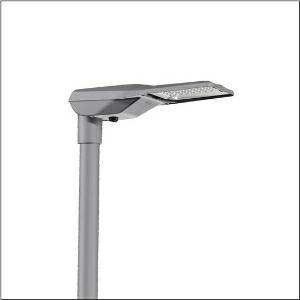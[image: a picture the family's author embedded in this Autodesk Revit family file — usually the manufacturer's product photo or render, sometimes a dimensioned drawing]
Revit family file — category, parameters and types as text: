
# Revit family: streetlight_sl_21_iq_mini___p0_8ab_5xe2r31u08gb_eb08
name_source: partatom
category: Lighting Fixtures
units: mm (PartAtom-declared; Revit-internal decimal feet)

## family parameters
Cut with Voids When Loaded = No
Host = Face
Light Source = No
Part Type = Normal
Room Calculation Point = No
Round Connector Dimension = Use Diameter
Shared = No

## types (1)
- --- (1 x LED, 5200 lm, 39.8 W, 3000K)
    Apparent Load = 40 VA
    CIE Flux Codes = 36 71 98 100 100
    Color Rendering = 70
    Color Temperature = 3000K
    Default Elevation = 1800 mm
    Description = Streetlight SL 21 iQ mini, mast luminaire, primary light control with lens, of PMMA, primary optical cover: cover, of toughened safety glass, transparent, light distribution: P0.8aB, light emission: direct distribution, primary light characteristic: asymmetric, installation type: post-top, side-entry, LED, High Power LED, rated luminous flux: 5.200lm, luminous efficacy: 131lm/W, light colour: 730, colour temperature: 3000K, control gear: iQ-Street Remote, D4i with power reduction, control: pre-setting: logarithmic dimming characteristic, Street-Remote, Auto-Match, Temp-Guard, Lumen-Switch, Night-Set, Smart-Wire, Light-Fading, Desk-Remote (wireless, voltage-free reading and setting of iQ features in the workshop via application-optimized NFC function/RFID function), optimised constant luminous flux control (CLO 2.0), mains connection: 220..240V, AC, 50/60Hz, start of lifetime: 40W, end of service life: 41W, reduction: 18W, luminaire housing, of diecast aluminium, powder-coated, SITECO metallic grey (DB 702S), corrosivity category C5 high according to DIN EN ISO 12944, please order mast flange separately, inclination adjustable: 0°, 5°, 10°, 15°, sealing non-destructively replaceable, multi-level sealing system, length: 628mm, width: 235mm, height: 110mm, mast flange for spigot size: 42mm (side-entry): 5XC10008XM4, 60/48mm (side-entry/post-top): 5XC10108XM2, 76/60mm (side-entry/post-top): 5XC10108XM1, mounting height: 4..8m, Smart Interface below, protection rating (complete): IP66, insulation class (complete): insulation class II (safety insulation), certification: CE, ENEC, ENEC+, VDE, impact resistance: IK10, permissible operating ambient temperature for outdoor applications: -40..+50°C, standard-compliant lighting for roads and squares, packaging unit: 1 piece

Light Distribution: P0.8aB
    Height = 110 mm
    Lamp = 1 x LED
    Lamp Light Flux = 5200 lm
    Lamp Power = 39.8 W
    Lamp count = 1
    Length = 625 mm
    Luminous efficacy = 131 lm/W
    Manufacturer = Siteco
    ModVariant = No
    Model = 5XE2R31U08GB
    Number of Poles = 1
    OnlyDefault = Yes
    Power Factor = 1
    Product Name = Streetlight SL 21 iQ mini | P0.8aB
    Product group = mast luminaire | pylon top
    ProductGroupID = 6100
    Protection Class = Protection class II
    Protection Degree = IP 66
    RLX_Detail_Level = 1
    RLX_Emergency_Light_Flux = 0 lm
    RLX_Emergency_Type = 0
    RLX_Emergency_Type_DB = No
    RlxData = <blob elided: 92461 chars, md5=9c527657>
    Socket = socket
    Standby Power = 0 W
    System Light Flux = 5200 lm
    System Power = 40 W
    Type Comments = factory setting: luminous flux: 100 % | dim-lin: 254 | 800 mA
    Type Image = l_1003516.jpg
    URL = http://relux.com
    VarID = @adj_083245
    Voltage = 0 V
    Weight = 0.00 kg
    Width = 234 mm

## geometry (parser evidence)
native form markers: Blend x4, Sweep x11
no freeform markers — native parametric forms only
